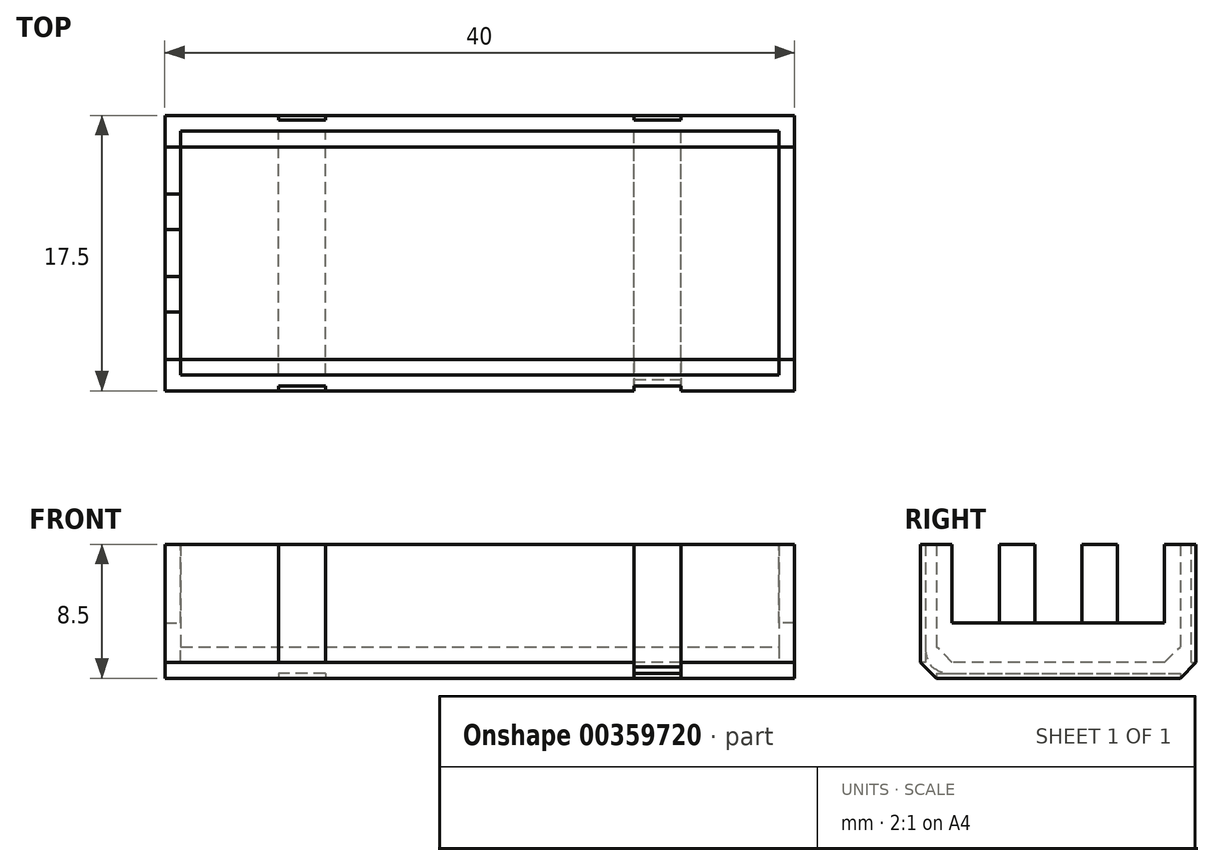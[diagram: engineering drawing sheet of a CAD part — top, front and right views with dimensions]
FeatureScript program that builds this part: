
annotation { "Feature Type Name" : "Feature", "Feature Type Description" : "" }
export const myFeature = defineFeature(function(context is Context, id is Id, definition is map)
    precondition{}
    {
        {
            var Q0;
            Q0=qCreatedBy(makeId("Top.planeOp"),FACE);
            var sketch = newSketch(context, id + "F0", { "sketchPlane" : qUnion([Q0])});
            skLineSegment(sketch, "E0.bottom", {"start": v(-85.67, 25.35) * mm, "end": v(-45.67, 25.35) * mm});
            skLineSegment(sketch, "E0.top", {"start": v(-85.67, 7.85) * mm, "end": v(-45.67, 7.85) * mm});
            skLineSegment(sketch, "E0.left", {"start": v(-85.67, 25.35) * mm, "end": v(-85.67, 7.85) * mm});
            skLineSegment(sketch, "E0.right", {"start": v(-45.67, 25.35) * mm, "end": v(-45.67, 7.85) * mm});
            skLineSegment(sketch, "E1", {"start": v(-65.67, 7.85) * mm, "end": v(-65.67, 25.35) * mm, "construction": true});
            skSolve(sketch);
        }
        {
            var Q0;
            Q0=qSketchRegion(id+"F0",true);
            extrude(context, id + "F1", {"entities" : qUnion([Q0]), "depth" : 8.5 * mm});
        }
        {
            var Q0;
            Q0=makeQuery(id+"F1.opExtrude","CAP_FACE",FACE,{"disambiguationData":[OSD([sQuery(id+"F0.wireOp",EDGE,"E0.bottom"),sQuery(id+"F0.wireOp",EDGE,"E0.top"),sQuery(id+"F0.wireOp",EDGE,"E0.left"),sQuery(id+"F0.wireOp",EDGE,"E0.right")])],"isStart":false});
            shell(context, id + "F2", {"entities" : qUnion([Q0]), "thickness" : 1 * mm});
        }
        {
            var Q0;
            Q0=makeQuery(id+"F1.opExtrude","CAP_FACE",FACE,{"disambiguationData":[OSD([sQuery(id+"F0.wireOp",EDGE,"E0.bottom"),sQuery(id+"F0.wireOp",EDGE,"E0.top"),sQuery(id+"F0.wireOp",EDGE,"E0.left"),sQuery(id+"F0.wireOp",EDGE,"E0.right")])],"isStart":false});
            var sketch = newSketch(context, id + "F3", { "sketchPlane" : qUnion([Q0])});
            skLineSegment(sketch, "E2", {"start": v(-85.67, 25.35) * mm, "end": v(-85.67, 23.35) * mm});
            skLineSegment(sketch, "E3", {"start": v(-85.67, 7.85) * mm, "end": v(-85.67, 9.85) * mm});
            skLineSegment(sketch, "E4.bottom", {"start": v(-85.67, 23.35) * mm, "end": v(-84.67, 23.35) * mm});
            skLineSegment(sketch, "E4.top", {"start": v(-85.67, 20.35) * mm, "end": v(-84.67, 20.35) * mm});
            skLineSegment(sketch, "E4.left", {"start": v(-85.67, 23.35) * mm, "end": v(-85.67, 20.35) * mm});
            skLineSegment(sketch, "E4.right", {"start": v(-84.67, 23.35) * mm, "end": v(-84.67, 20.35) * mm});
            skLineSegment(sketch, "E5.bottom", {"start": v(-85.67, 9.85) * mm, "end": v(-84.67, 9.85) * mm});
            skLineSegment(sketch, "E5.top", {"start": v(-85.67, 12.85) * mm, "end": v(-84.67, 12.85) * mm});
            skLineSegment(sketch, "E5.left", {"start": v(-85.67, 9.85) * mm, "end": v(-85.67, 12.85) * mm});
            skLineSegment(sketch, "E5.right", {"start": v(-84.67, 9.85) * mm, "end": v(-84.67, 12.85) * mm});
            skLineSegment(sketch, "E6.bottom", {"start": v(-85.67, 18.1) * mm, "end": v(-84.67, 18.1) * mm});
            skLineSegment(sketch, "E6.top", {"start": v(-85.67, 15.1) * mm, "end": v(-84.67, 15.1) * mm});
            skLineSegment(sketch, "E6.left", {"start": v(-85.67, 18.1) * mm, "end": v(-85.67, 15.1) * mm});
            skLineSegment(sketch, "E6.right", {"start": v(-84.67, 18.1) * mm, "end": v(-84.67, 15.1) * mm});
            skPoint(sketch, "E7", {"position": v(-84.67, 16.6) * mm});
            skPoint(sketch, "E8", {"position": v(-46.67, 16.6) * mm});
            skLineSegment(sketch, "E9", {"start": v(-65.67, 24.35) * mm, "end": v(-65.67, 8.85) * mm, "construction": true});
            skLineSegment(sketch, "E10.MirrorCS", {"start": v(-45.67, 23.35) * mm, "end": v(-46.67, 23.35) * mm});
            skLineSegment(sketch, "E11.MirrorCS", {"start": v(-45.67, 20.35) * mm, "end": v(-46.67, 20.35) * mm});
            skLineSegment(sketch, "E12.MirrorCS", {"start": v(-45.67, 23.35) * mm, "end": v(-45.67, 20.35) * mm});
            skLineSegment(sketch, "E13.MirrorCS", {"start": v(-46.67, 23.35) * mm, "end": v(-46.67, 20.35) * mm});
            skLineSegment(sketch, "E14.MirrorCS", {"start": v(-45.67, 9.85) * mm, "end": v(-46.67, 9.85) * mm});
            skLineSegment(sketch, "E15.MirrorCS", {"start": v(-45.67, 12.85) * mm, "end": v(-46.67, 12.85) * mm});
            skLineSegment(sketch, "E16.MirrorCS", {"start": v(-45.67, 9.85) * mm, "end": v(-45.67, 12.85) * mm});
            skLineSegment(sketch, "E17.MirrorCS", {"start": v(-46.67, 9.85) * mm, "end": v(-46.67, 12.85) * mm});
            skLineSegment(sketch, "E18.MirrorCS", {"start": v(-45.67, 18.1) * mm, "end": v(-45.67, 15.1) * mm});
            skLineSegment(sketch, "E19.MirrorCS", {"start": v(-46.67, 18.1) * mm, "end": v(-46.67, 15.1) * mm});
            skLineSegment(sketch, "E20.MirrorCS", {"start": v(-45.67, 15.1) * mm, "end": v(-46.67, 15.1) * mm});
            skLineSegment(sketch, "E21.MirrorCS", {"start": v(-45.67, 18.1) * mm, "end": v(-46.67, 18.1) * mm});
            skSolve(sketch);
        }
        {
            var Q0;
            Q0=makeQuery(id+"F3.imprint","IMPRINT",FACE,{"disambiguationData":[TD([[makeQuery(id+"F3.imprint","IMPRINT",EDGE,{"derivedFrom":sQuery(id+"F3.wireOp",EDGE,"E4.bottom")}),-1.0]])]});
            var Q1;
            Q1=makeQuery(id+"F3.imprint","IMPRINT",FACE,{"disambiguationData":[TD([[makeQuery(id+"F3.imprint","IMPRINT",EDGE,{"derivedFrom":sQuery(id+"F3.wireOp",EDGE,"E6.bottom")}),-1.0]])]});
            var Q2;
            Q2=makeQuery(id+"F3.imprint","IMPRINT",FACE,{"disambiguationData":[TD([[makeQuery(id+"F3.imprint","IMPRINT",EDGE,{"derivedFrom":sQuery(id+"F3.wireOp",EDGE,"E5.bottom")}),1.0]])]});
            var Q3;
            Q3=makeQuery(id+"F3.imprint","IMPRINT",FACE,{"disambiguationData":[TD([[makeQuery(id+"F3.imprint","IMPRINT",EDGE,{"derivedFrom":sQuery(id+"F3.wireOp",EDGE,"E14.MirrorCS")}),-1.0]])]});
            var Q4;
            Q4=makeQuery(id+"F3.imprint","IMPRINT",FACE,{"disambiguationData":[TD([[makeQuery(id+"F3.imprint","IMPRINT",EDGE,{"derivedFrom":sQuery(id+"F3.wireOp",EDGE,"E18.MirrorCS")}),-1.0]])]});
            var Q5;
            Q5=makeQuery(id+"F3.imprint","IMPRINT",FACE,{"disambiguationData":[TD([[makeQuery(id+"F3.imprint","IMPRINT",EDGE,{"derivedFrom":sQuery(id+"F3.wireOp",EDGE,"E10.MirrorCS")}),1.0]])]});
            extrude(context, id + "F4", {"entities" : qUnion([Q0, Q1, Q2, Q3, Q4, Q5]), "operationType" : NewBodyOperationType.REMOVE, "oppositeDirection" : true, "depth" : 5 * mm});
        }
        {
            var Q0;
            Q0=makeQuery(id+"F1.opExtrude","CAP_EDGE",EDGE,{"disambiguationData":[OSD([sQuery(id+"F0.wireOp",EDGE,"E0.top")])],"isStart":true});
            var Q1;
            {var subQ0=sQuery(id+"F0.wireOp",EDGE,"E0.top");var subQ1=sQuery(id+"F0.wireOp",EDGE,"E0.right");Q1=makeQuery(id+"F6hiMXC0ifSG0O5_1.opFillet","BLEND_EDGE",EDGE,{"blendedFrom":[makeQuery(id+"FY9jGdD6YKkP4tm_1.opChamfer","BLEND_EDGE",EDGE,{"blendedFrom":[makeQuery(id+"F1.opExtrude","CAP_EDGE",EDGE,{"disambiguationData":[OSD([subQ1])],"isStart":true}),makeQuery(id+"F1.opExtrude","CAP_FACE",FACE,{"disambiguationData":[OSD([sQuery(id+"F0.wireOp",EDGE,"E0.bottom"),subQ0,sQuery(id+"F0.wireOp",EDGE,"E0.left"),subQ1])],"isStart":true})],"blendedInto":[makeQuery(id+"F1.opExtrude","CAP_FACE",FACE,{"disambiguationData":[OSD([sQuery(id+"F0.wireOp",EDGE,"E0.bottom"),subQ0,sQuery(id+"F0.wireOp",EDGE,"E0.left"),subQ1])],"isStart":true})]}),makeQuery(id+"F1.opExtrude","SWEPT_FACE",FACE,{"disambiguationData":[OSD([subQ0])]})],"blendedInto":[makeQuery(id+"F1.opExtrude","SWEPT_FACE",FACE,{"disambiguationData":[OSD([subQ0])]})]});}
            var Q2;
            Q2=makeQuery(id+"FY9jGdD6YKkP4tm_1.opChamfer","BLEND_EDGE",EDGE,{"blendedFrom":[makeQuery(id+"F1.opExtrude","CAP_EDGE",EDGE,{"disambiguationData":[OSD([sQuery(id+"F0.wireOp",EDGE,"E0.right")])],"isStart":true}),makeQuery(id+"F1.opExtrude","SWEPT_FACE",FACE,{"disambiguationData":[OSD([sQuery(id+"F0.wireOp",EDGE,"E0.top")])]})],"blendedInto":[makeQuery(id+"F1.opExtrude","SWEPT_FACE",FACE,{"disambiguationData":[OSD([sQuery(id+"F0.wireOp",EDGE,"E0.top")])]})]});
            var Q3;
            {var subQ0=sQuery(id+"F0.wireOp",EDGE,"E0.top");var subQ1=sQuery(id+"F0.wireOp",EDGE,"E0.left");Q3=makeQuery(id+"F6hiMXC0ifSG0O5_1.opFillet","BLEND_EDGE",EDGE,{"blendedFrom":[makeQuery(id+"FY9jGdD6YKkP4tm_1.opChamfer","BLEND_EDGE",EDGE,{"blendedFrom":[makeQuery(id+"F1.opExtrude","CAP_EDGE",EDGE,{"disambiguationData":[OSD([subQ1])],"isStart":true}),makeQuery(id+"F1.opExtrude","CAP_FACE",FACE,{"disambiguationData":[OSD([sQuery(id+"F0.wireOp",EDGE,"E0.bottom"),subQ0,subQ1,sQuery(id+"F0.wireOp",EDGE,"E0.right")])],"isStart":true})],"blendedInto":[makeQuery(id+"F1.opExtrude","CAP_FACE",FACE,{"disambiguationData":[OSD([sQuery(id+"F0.wireOp",EDGE,"E0.bottom"),subQ0,subQ1,sQuery(id+"F0.wireOp",EDGE,"E0.right")])],"isStart":true})]}),makeQuery(id+"F1.opExtrude","SWEPT_FACE",FACE,{"disambiguationData":[OSD([subQ0])]})],"blendedInto":[makeQuery(id+"F1.opExtrude","SWEPT_FACE",FACE,{"disambiguationData":[OSD([subQ0])]})]});}
            var Q4;
            Q4=makeQuery(id+"FY9jGdD6YKkP4tm_1.opChamfer","BLEND_EDGE",EDGE,{"blendedFrom":[makeQuery(id+"F1.opExtrude","CAP_EDGE",EDGE,{"disambiguationData":[OSD([sQuery(id+"F0.wireOp",EDGE,"E0.left")])],"isStart":true}),makeQuery(id+"F1.opExtrude","SWEPT_FACE",FACE,{"disambiguationData":[OSD([sQuery(id+"F0.wireOp",EDGE,"E0.top")])]})],"blendedInto":[makeQuery(id+"F1.opExtrude","SWEPT_FACE",FACE,{"disambiguationData":[OSD([sQuery(id+"F0.wireOp",EDGE,"E0.top")])]})]});
            var Q5;
            Q5=makeQuery(id+"FY9jGdD6YKkP4tm_1.opChamfer","BLEND_EDGE",EDGE,{"blendedFrom":[makeQuery(id+"F1.opExtrude","CAP_EDGE",EDGE,{"disambiguationData":[OSD([sQuery(id+"F0.wireOp",EDGE,"E0.right")])],"isStart":true}),makeQuery(id+"F1.opExtrude","SWEPT_FACE",FACE,{"disambiguationData":[OSD([sQuery(id+"F0.wireOp",EDGE,"E0.bottom")])]})],"blendedInto":[makeQuery(id+"F1.opExtrude","SWEPT_FACE",FACE,{"disambiguationData":[OSD([sQuery(id+"F0.wireOp",EDGE,"E0.bottom")])]})]});
            var Q6;
            {var subQ0=sQuery(id+"F0.wireOp",EDGE,"E0.bottom");var subQ1=sQuery(id+"F0.wireOp",EDGE,"E0.right");Q6=makeQuery(id+"F6hiMXC0ifSG0O5_1.opFillet","BLEND_EDGE",EDGE,{"blendedFrom":[makeQuery(id+"FY9jGdD6YKkP4tm_1.opChamfer","BLEND_EDGE",EDGE,{"blendedFrom":[makeQuery(id+"F1.opExtrude","CAP_EDGE",EDGE,{"disambiguationData":[OSD([subQ1])],"isStart":true}),makeQuery(id+"F1.opExtrude","CAP_FACE",FACE,{"disambiguationData":[OSD([subQ0,sQuery(id+"F0.wireOp",EDGE,"E0.top"),sQuery(id+"F0.wireOp",EDGE,"E0.left"),subQ1])],"isStart":true})],"blendedInto":[makeQuery(id+"F1.opExtrude","CAP_FACE",FACE,{"disambiguationData":[OSD([subQ0,sQuery(id+"F0.wireOp",EDGE,"E0.top"),sQuery(id+"F0.wireOp",EDGE,"E0.left"),subQ1])],"isStart":true})]}),makeQuery(id+"F1.opExtrude","SWEPT_FACE",FACE,{"disambiguationData":[OSD([subQ0])]})],"blendedInto":[makeQuery(id+"F1.opExtrude","SWEPT_FACE",FACE,{"disambiguationData":[OSD([subQ0])]})]});}
            var Q7;
            Q7=makeQuery(id+"F1.opExtrude","CAP_EDGE",EDGE,{"disambiguationData":[OSD([sQuery(id+"F0.wireOp",EDGE,"E0.bottom")])],"isStart":true});
            var Q8;
            {var subQ0=sQuery(id+"F0.wireOp",EDGE,"E0.bottom");var subQ1=sQuery(id+"F0.wireOp",EDGE,"E0.left");Q8=makeQuery(id+"F6hiMXC0ifSG0O5_1.opFillet","BLEND_EDGE",EDGE,{"blendedFrom":[makeQuery(id+"FY9jGdD6YKkP4tm_1.opChamfer","BLEND_EDGE",EDGE,{"blendedFrom":[makeQuery(id+"F1.opExtrude","CAP_EDGE",EDGE,{"disambiguationData":[OSD([subQ1])],"isStart":true}),makeQuery(id+"F1.opExtrude","CAP_FACE",FACE,{"disambiguationData":[OSD([subQ0,sQuery(id+"F0.wireOp",EDGE,"E0.top"),subQ1,sQuery(id+"F0.wireOp",EDGE,"E0.right")])],"isStart":true})],"blendedInto":[makeQuery(id+"F1.opExtrude","CAP_FACE",FACE,{"disambiguationData":[OSD([subQ0,sQuery(id+"F0.wireOp",EDGE,"E0.top"),subQ1,sQuery(id+"F0.wireOp",EDGE,"E0.right")])],"isStart":true})]}),makeQuery(id+"F1.opExtrude","SWEPT_FACE",FACE,{"disambiguationData":[OSD([subQ0])]})],"blendedInto":[makeQuery(id+"F1.opExtrude","SWEPT_FACE",FACE,{"disambiguationData":[OSD([subQ0])]})]});}
            var Q9;
            Q9=makeQuery(id+"FY9jGdD6YKkP4tm_1.opChamfer","BLEND_EDGE",EDGE,{"blendedFrom":[makeQuery(id+"F1.opExtrude","CAP_EDGE",EDGE,{"disambiguationData":[OSD([sQuery(id+"F0.wireOp",EDGE,"E0.left")])],"isStart":true}),makeQuery(id+"F1.opExtrude","SWEPT_FACE",FACE,{"disambiguationData":[OSD([sQuery(id+"F0.wireOp",EDGE,"E0.bottom")])]})],"blendedInto":[makeQuery(id+"F1.opExtrude","SWEPT_FACE",FACE,{"disambiguationData":[OSD([sQuery(id+"F0.wireOp",EDGE,"E0.bottom")])]})]});
            chamfer(context, id + "F5", {"entities" : qUnion([Q0, Q1, Q2, Q3, Q4, Q5, Q6, Q7, Q8, Q9]), "width" : 1 * mm, "tangentPropagation" : true});
        }
        {
            var Q0;
            Q0=makeQuery(id+"F1.opExtrude","CAP_FACE",FACE,{"disambiguationData":[OSD([sQuery(id+"F0.wireOp",EDGE,"E0.bottom"),sQuery(id+"F0.wireOp",EDGE,"E0.top"),sQuery(id+"F0.wireOp",EDGE,"E0.left"),sQuery(id+"F0.wireOp",EDGE,"E0.right")])],"isStart":true});
            var sketch = newSketch(context, id + "F6", { "sketchPlane" : qUnion([Q0])});
            skLineSegment(sketch, "E22.bottom", {"start": v(-78.46, -8.85) * mm, "end": v(-75.46, -8.85) * mm});
            skLineSegment(sketch, "E22.top", {"start": v(-78.46, -24.35) * mm, "end": v(-75.46, -24.35) * mm});
            skLineSegment(sketch, "E22.left", {"start": v(-78.46, -8.85) * mm, "end": v(-78.46, -24.35) * mm});
            skLineSegment(sketch, "E22.right", {"start": v(-75.46, -8.85) * mm, "end": v(-75.46, -24.35) * mm});
            skLineSegment(sketch, "E23.MirrorCS", {"start": v(-52.88, -8.85) * mm, "end": v(-52.88, -24.35) * mm});
            skLineSegment(sketch, "E24.MirrorCS", {"start": v(-52.88, -8.85) * mm, "end": v(-55.88, -8.85) * mm});
            skLineSegment(sketch, "E25.MirrorCS", {"start": v(-52.88, -24.35) * mm, "end": v(-55.88, -24.35) * mm});
            skLineSegment(sketch, "E26.MirrorCS", {"start": v(-55.88, -8.85) * mm, "end": v(-55.88, -24.35) * mm});
            skSolve(sketch);
        }
        {
            var Q0;
            Q0=makeQuery(id+"F5.opChamfer","BLEND_FACE",FACE,{"disambiguationData":[OSD([sQuery(id+"F0.wireOp",EDGE,"E0.bottom")])]});
            var sketch = newSketch(context, id + "F7", { "sketchPlane" : qUnion([Q0])});
            skLineSegment(sketch, "E27.0.0", {"start": v(-75.46, -17.22) * mm, "end": v(-75.46, -6.26) * mm});
            skLineSegment(sketch, "E27.0.1", {"start": v(-75.46, -6.26) * mm, "end": v(-78.46, -6.26) * mm});
            skLineSegment(sketch, "E27.0.2", {"start": v(-78.46, -6.26) * mm, "end": v(-78.46, -17.22) * mm});
            skLineSegment(sketch, "E27.0.3", {"start": v(-78.46, -17.22) * mm, "end": v(-75.46, -17.22) * mm});
            skLineSegment(sketch, "E28.left", {"start": v(-78.46, -17.22) * mm, "end": v(-78.46, -17.22) * mm});
            skLineSegment(sketch, "E28.right", {"start": v(-75.46, -17.22) * mm, "end": v(-75.46, -17.22) * mm});
            skLineSegment(sketch, "E29.bottom", {"start": v(-75.46, -18.63) * mm, "end": v(-78.46, -18.63) * mm});
            skLineSegment(sketch, "E29.top", {"start": v(-75.46, -17.22) * mm, "end": v(-78.46, -17.22) * mm});
            skLineSegment(sketch, "E29.left", {"start": v(-75.46, -18.63) * mm, "end": v(-75.46, -17.22) * mm});
            skLineSegment(sketch, "E29.right", {"start": v(-78.46, -18.63) * mm, "end": v(-78.46, -17.22) * mm});
            skLineSegment(sketch, "E30.MirrorCS", {"start": v(-52.88, -17.22) * mm, "end": v(-55.88, -17.22) * mm});
            skLineSegment(sketch, "E31.MirrorCS", {"start": v(-52.88, -18.63) * mm, "end": v(-52.88, -17.22) * mm});
            skLineSegment(sketch, "E32.MirrorCS", {"start": v(-55.88, -18.63) * mm, "end": v(-55.88, -17.22) * mm});
            skLineSegment(sketch, "E33.MirrorCS", {"start": v(-55.88, -18.63) * mm, "end": v(-52.88, -18.63) * mm});
            skLineSegment(sketch, "E34.MirrorCS", {"start": v(-55.88, -17.22) * mm, "end": v(-52.88, -17.22) * mm});
            skSolve(sketch);
        }
        {
            var Q0;
            Q0=makeQuery(id+"F1.opExtrude","SWEPT_FACE",FACE,{"disambiguationData":[OSD([sQuery(id+"F0.wireOp",EDGE,"E0.bottom")])]});
            var sketch = newSketch(context, id + "F8", { "sketchPlane" : qUnion([Q0])});
            skLineSegment(sketch, "E35.0.0", {"start": v(78.46, 0) * mm, "end": v(78.46, 1) * mm});
            skLineSegment(sketch, "E35.0.1", {"start": v(78.46, 1) * mm, "end": v(75.46, 1) * mm});
            skLineSegment(sketch, "E35.0.2", {"start": v(75.46, 1) * mm, "end": v(75.46, 0) * mm});
            skLineSegment(sketch, "E35.0.3", {"start": v(75.46, 0) * mm, "end": v(78.46, 0) * mm});
            skLineSegment(sketch, "E36.top", {"start": v(78.46, 8.5) * mm, "end": v(75.46, 8.5) * mm});
            skLineSegment(sketch, "E36.left", {"start": v(78.46, 1) * mm, "end": v(78.46, 8.5) * mm});
            skLineSegment(sketch, "E36.right", {"start": v(75.46, 1) * mm, "end": v(75.46, 8.5) * mm});
            skLineSegment(sketch, "E37", {"start": v(65.67, 1) * mm, "end": v(65.67, 8.5) * mm, "construction": true});
            skLineSegment(sketch, "E38.MirrorCS", {"start": v(52.88, 1) * mm, "end": v(55.88, 1) * mm});
            skLineSegment(sketch, "E39.MirrorCS", {"start": v(52.88, 1) * mm, "end": v(52.88, 8.5) * mm});
            skLineSegment(sketch, "E40.MirrorCS", {"start": v(55.88, 1) * mm, "end": v(55.88, 8.5) * mm});
            skLineSegment(sketch, "E41.MirrorCS", {"start": v(52.88, 8.5) * mm, "end": v(55.88, 8.5) * mm});
            skSolve(sketch);
        }
        {
            var Q0;
            Q0=makeQuery(id+"F1.opExtrude","SWEPT_FACE",FACE,{"disambiguationData":[OSD([sQuery(id+"F0.wireOp",EDGE,"E0.top")])]});
            var sketch = newSketch(context, id + "F9", { "sketchPlane" : qUnion([Q0])});
            skLineSegment(sketch, "E42.0.0", {"start": v(-75.46, 8.5) * mm, "end": v(-75.46, 1) * mm});
            skLineSegment(sketch, "E42.0.1", {"start": v(-75.46, 1) * mm, "end": v(-78.46, 1) * mm});
            skLineSegment(sketch, "E42.0.2", {"start": v(-78.46, 1) * mm, "end": v(-78.46, 8.5) * mm});
            skLineSegment(sketch, "E42.0.3", {"start": v(-78.46, 8.5) * mm, "end": v(-75.46, 8.5) * mm});
            skLineSegment(sketch, "E43", {"start": v(-65.67, 1) * mm, "end": v(-65.67, 8.5) * mm, "construction": true});
            skLineSegment(sketch, "E44.MirrorCS", {"start": v(-55.88, 1) * mm, "end": v(-52.88, 1) * mm});
            skLineSegment(sketch, "E45.MirrorCS", {"start": v(-55.88, 8.5) * mm, "end": v(-55.88, 1) * mm});
            skLineSegment(sketch, "E46.MirrorCS", {"start": v(-52.88, 8.5) * mm, "end": v(-55.88, 8.5) * mm});
            skLineSegment(sketch, "E47.MirrorCS", {"start": v(-52.88, 1) * mm, "end": v(-52.88, 8.5) * mm});
            skSolve(sketch);
        }
        {
            var Q0;
            Q0=makeQuery(id+"F5.opChamfer","BLEND_FACE",FACE,{"disambiguationData":[OSD([sQuery(id+"F0.wireOp",EDGE,"E0.top")])]});
            var sketch = newSketch(context, id + "F10", { "sketchPlane" : qUnion([Q0])});
            skLineSegment(sketch, "E48.0.0", {"start": v(-78.46, 0.46) * mm, "end": v(-78.46, -4.84) * mm});
            skLineSegment(sketch, "E48.0.1", {"start": v(-78.46, -4.84) * mm, "end": v(-75.46, -4.84) * mm});
            skLineSegment(sketch, "E48.0.2", {"start": v(-75.46, -4.84) * mm, "end": v(-75.46, 0.46) * mm});
            skLineSegment(sketch, "E48.0.3", {"start": v(-75.46, 0.46) * mm, "end": v(-78.46, 0.46) * mm});
            skLineSegment(sketch, "E49.bottom", {"start": v(-75.46, -4.84) * mm, "end": v(-78.46, -4.84) * mm});
            skLineSegment(sketch, "E49.top", {"start": v(-75.46, -6.26) * mm, "end": v(-78.46, -6.26) * mm});
            skLineSegment(sketch, "E49.left", {"start": v(-75.46, -4.84) * mm, "end": v(-75.46, -6.26) * mm});
            skLineSegment(sketch, "E49.right", {"start": v(-78.46, -4.84) * mm, "end": v(-78.46, -6.26) * mm});
            skLineSegment(sketch, "E50.MirrorCS", {"start": v(-52.88, -4.84) * mm, "end": v(-55.88, -4.84) * mm});
            skLineSegment(sketch, "E51.MirrorCS", {"start": v(-52.88, -4.84) * mm, "end": v(-52.88, -6.26) * mm});
            skLineSegment(sketch, "E52.MirrorCS", {"start": v(-55.88, -4.84) * mm, "end": v(-55.88, -6.26) * mm});
            skLineSegment(sketch, "E53.MirrorCS", {"start": v(-55.88, -4.84) * mm, "end": v(-52.88, -4.84) * mm});
            skLineSegment(sketch, "E54.MirrorCS", {"start": v(-55.88, -6.26) * mm, "end": v(-52.88, -6.26) * mm});
            skSolve(sketch);
        }
        {
            var Q0;
            Q0=makeQuery(id+"F8.imprint","IMPRINT",FACE,{"disambiguationData":[TD([[makeQuery(id+"F8.imprint","IMPRINT",EDGE,{"derivedFrom":sQuery(id+"F8.wireOp",EDGE,"E35.0.1")}),1.0]])]});
            var Q1;
            Q1=makeQuery(id+"F8.imprint","IMPRINT",FACE,{"disambiguationData":[TD([[makeQuery(id+"F8.imprint","IMPRINT",EDGE,{"derivedFrom":sQuery(id+"F8.wireOp",EDGE,"E39.MirrorCS")}),-1.0]])]});
            extrude(context, id + "F11", {"entities" : qUnion([Q0, Q1]), "operationType" : NewBodyOperationType.REMOVE, "oppositeDirection" : true, "depth" : .3 * mm});
        }
        {
            var Q0;
            Q0=makeQuery(id+"F7.imprint","IMPRINT",FACE,{"disambiguationData":[TD([[makeQuery(id+"F7.imprint","IMPRINT",EDGE,{"derivedFrom":sQuery(id+"F7.wireOp",EDGE,"E29.bottom")}),-1.0]])]});
            var Q1;
            Q1=makeQuery(id+"F7.imprint","IMPRINT",FACE,{"disambiguationData":[TD([[makeQuery(id+"F7.imprint","IMPRINT",EDGE,{"derivedFrom":sQuery(id+"F7.wireOp",EDGE,"E31.MirrorCS")}),1.0]])]});
            extrude(context, id + "F12", {"entities" : qUnion([Q0, Q1]), "operationType" : NewBodyOperationType.REMOVE, "oppositeDirection" : true, "depth" : 0.3 * mm});
        }
        {
            var Q0;
            Q0=makeQuery(id+"F6.imprint","IMPRINT",FACE,{"disambiguationData":[TD([[makeQuery(id+"F6.imprint","IMPRINT",EDGE,{"derivedFrom":sQuery(id+"F6.wireOp",EDGE,"E22.bottom")}),1.0]])]});
            var Q1;
            Q1=makeQuery(id+"F6.imprint","IMPRINT",FACE,{"disambiguationData":[TD([[makeQuery(id+"F6.imprint","IMPRINT",EDGE,{"derivedFrom":sQuery(id+"F6.wireOp",EDGE,"E23.MirrorCS")}),-1.0]])]});
            extrude(context, id + "F13", {"entities" : qUnion([Q0, Q1]), "operationType" : NewBodyOperationType.REMOVE, "oppositeDirection" : true, "depth" : 0.3 * mm});
        }
        {
            var Q0;
            Q0=makeQuery(id+"F9.imprint","IMPRINT",FACE,{"disambiguationData":[TD([[makeQuery(id+"F9.imprint","IMPRINT",EDGE,{"derivedFrom":sQuery(id+"F9.wireOp",EDGE,"E42.0.0")}),-1.0]])]});
            var Q1;
            Q1=makeQuery(id+"F9.imprint","IMPRINT",FACE,{"disambiguationData":[TD([[makeQuery(id+"F9.imprint","IMPRINT",EDGE,{"derivedFrom":sQuery(id+"F9.wireOp",EDGE,"E44.MirrorCS")}),1.0]])]});
            extrude(context, id + "F14", {"entities" : qUnion([Q0, Q1]), "operationType" : NewBodyOperationType.REMOVE, "oppositeDirection" : true, "depth" : 0.3 * mm});
        }
        {
            var Q0;
            Q0=makeQuery(id+"F10.imprint","IMPRINT",FACE,{"disambiguationData":[TD([[makeQuery(id+"F10.imprint","IMPRINT",EDGE,{"derivedFrom":sQuery(id+"F10.wireOp",EDGE,"E49.bottom")}),-1.0]])]});
            var Q1;
            Q1=makeQuery(id+"F10.imprint","IMPRINT",FACE,{"disambiguationData":[TD([[makeQuery(id+"F10.imprint","IMPRINT",EDGE,{"derivedFrom":sQuery(id+"F10.wireOp",EDGE,"E51.MirrorCS")}),-1.0]])]});
            extrude(context, id + "F15", {"entities" : qUnion([Q0, Q1]), "operationType" : NewBodyOperationType.REMOVE, "oppositeDirection" : true, "depth" : 0.3 * mm});
        }
        {
            var Q0;
            Q0=makeQuery(id+"F15.boolean.opBoolean","INTERSECT",EDGE,{"derivedFrom":[makeQuery(id+"F14.boolean.opBoolean","COPY",FACE,{"derivedFrom":makeQuery(id+"F14.opExtrude","CAP_FACE",FACE,{"disambiguationData":[OSD([sQuery(id+"F9.wireOp",EDGE,"E44.MirrorCS"),sQuery(id+"F9.wireOp",EDGE,"E45.MirrorCS"),sQuery(id+"F9.wireOp",EDGE,"E46.MirrorCS"),sQuery(id+"F9.wireOp",EDGE,"E47.MirrorCS")])],"isStart":false})}),makeQuery(id+"F15.opExtrude","CAP_FACE",FACE,{"disambiguationData":[OSD([sQuery(id+"F10.wireOp",EDGE,"E51.MirrorCS"),sQuery(id+"F10.wireOp",EDGE,"E52.MirrorCS"),sQuery(id+"F10.wireOp",EDGE,"E53.MirrorCS"),sQuery(id+"F10.wireOp",EDGE,"E54.MirrorCS")])],"isStart":false})]});
            var Q1;
            Q1=makeQuery(id+"F15.boolean.opBoolean","INTERSECT",EDGE,{"derivedFrom":[makeQuery(id+"F13.boolean.opBoolean","COPY",FACE,{"derivedFrom":makeQuery(id+"F13.opExtrude","CAP_FACE",FACE,{"disambiguationData":[OSD([sQuery(id+"F6.wireOp",EDGE,"E23.MirrorCS"),sQuery(id+"F6.wireOp",EDGE,"E24.MirrorCS"),sQuery(id+"F6.wireOp",EDGE,"E25.MirrorCS"),sQuery(id+"F6.wireOp",EDGE,"E26.MirrorCS")])],"isStart":false})}),makeQuery(id+"F15.opExtrude","CAP_FACE",FACE,{"disambiguationData":[OSD([sQuery(id+"F10.wireOp",EDGE,"E51.MirrorCS"),sQuery(id+"F10.wireOp",EDGE,"E52.MirrorCS"),sQuery(id+"F10.wireOp",EDGE,"E53.MirrorCS"),sQuery(id+"F10.wireOp",EDGE,"E54.MirrorCS")])],"isStart":false})]});
            var Q2;
            Q2=makeQuery(id+"F15.boolean.opBoolean","INTERSECT",EDGE,{"derivedFrom":[makeQuery(id+"F13.boolean.opBoolean","COPY",FACE,{"derivedFrom":makeQuery(id+"F13.opExtrude","CAP_FACE",FACE,{"disambiguationData":[OSD([sQuery(id+"F6.wireOp",EDGE,"E22.bottom"),sQuery(id+"F6.wireOp",EDGE,"E22.top"),sQuery(id+"F6.wireOp",EDGE,"E22.left"),sQuery(id+"F6.wireOp",EDGE,"E22.right")])],"isStart":false})}),makeQuery(id+"F15.opExtrude","CAP_FACE",FACE,{"disambiguationData":[OSD([sQuery(id+"F10.wireOp",EDGE,"E49.bottom"),sQuery(id+"F10.wireOp",EDGE,"E49.top"),sQuery(id+"F10.wireOp",EDGE,"E49.left"),sQuery(id+"F10.wireOp",EDGE,"E49.right")])],"isStart":false})]});
            var Q3;
            Q3=makeQuery(id+"F15.boolean.opBoolean","INTERSECT",EDGE,{"derivedFrom":[makeQuery(id+"F14.boolean.opBoolean","COPY",FACE,{"derivedFrom":makeQuery(id+"F14.opExtrude","CAP_FACE",FACE,{"disambiguationData":[OSD([sQuery(id+"F9.wireOp",EDGE,"E42.0.0"),sQuery(id+"F9.wireOp",EDGE,"E42.0.1"),sQuery(id+"F9.wireOp",EDGE,"E42.0.2"),sQuery(id+"F9.wireOp",EDGE,"E42.0.3")])],"isStart":false})}),makeQuery(id+"F15.opExtrude","CAP_FACE",FACE,{"disambiguationData":[OSD([sQuery(id+"F10.wireOp",EDGE,"E49.bottom"),sQuery(id+"F10.wireOp",EDGE,"E49.top"),sQuery(id+"F10.wireOp",EDGE,"E49.left"),sQuery(id+"F10.wireOp",EDGE,"E49.right")])],"isStart":false})]});
            var Q4;
            Q4=makeQuery(id+"F13.boolean.opBoolean","INTERSECT",EDGE,{"derivedFrom":[makeQuery(id+"F12.boolean.opBoolean","COPY",FACE,{"derivedFrom":makeQuery(id+"F12.opExtrude","CAP_FACE",FACE,{"disambiguationData":[OSD([sQuery(id+"F7.wireOp",EDGE,"E29.bottom"),sQuery(id+"F7.wireOp",EDGE,"E29.top"),sQuery(id+"F7.wireOp",EDGE,"E29.left"),sQuery(id+"F7.wireOp",EDGE,"E29.right")])],"isStart":false})}),makeQuery(id+"F13.opExtrude","CAP_FACE",FACE,{"disambiguationData":[OSD([sQuery(id+"F6.wireOp",EDGE,"E22.bottom"),sQuery(id+"F6.wireOp",EDGE,"E22.top"),sQuery(id+"F6.wireOp",EDGE,"E22.left"),sQuery(id+"F6.wireOp",EDGE,"E22.right")])],"isStart":false})]});
            var Q5;
            Q5=makeQuery(id+"F12.boolean.opBoolean","INTERSECT",EDGE,{"derivedFrom":[makeQuery(id+"F11.boolean.opBoolean","COPY",FACE,{"derivedFrom":makeQuery(id+"F11.opExtrude","CAP_FACE",FACE,{"disambiguationData":[OSD([sQuery(id+"F8.wireOp",EDGE,"E35.0.1"),sQuery(id+"F8.wireOp",EDGE,"E36.top"),sQuery(id+"F8.wireOp",EDGE,"E36.left"),sQuery(id+"F8.wireOp",EDGE,"E36.right")])],"isStart":false})}),makeQuery(id+"F12.opExtrude","CAP_FACE",FACE,{"disambiguationData":[OSD([sQuery(id+"F7.wireOp",EDGE,"E29.bottom"),sQuery(id+"F7.wireOp",EDGE,"E29.top"),sQuery(id+"F7.wireOp",EDGE,"E29.left"),sQuery(id+"F7.wireOp",EDGE,"E29.right")])],"isStart":false})]});
            var Q6;
            Q6=makeQuery(id+"F12.boolean.opBoolean","INTERSECT",EDGE,{"derivedFrom":[makeQuery(id+"F11.boolean.opBoolean","COPY",FACE,{"derivedFrom":makeQuery(id+"F11.opExtrude","CAP_FACE",FACE,{"disambiguationData":[OSD([sQuery(id+"F8.wireOp",EDGE,"E39.MirrorCS"),sQuery(id+"F8.wireOp",EDGE,"E40.MirrorCS"),sQuery(id+"F8.wireOp",EDGE,"E38.MirrorCS"),sQuery(id+"F8.wireOp",EDGE,"E41.MirrorCS")])],"isStart":false})}),makeQuery(id+"F12.opExtrude","CAP_FACE",FACE,{"disambiguationData":[OSD([sQuery(id+"F7.wireOp",EDGE,"E31.MirrorCS"),sQuery(id+"F7.wireOp",EDGE,"E32.MirrorCS"),sQuery(id+"F7.wireOp",EDGE,"E33.MirrorCS"),sQuery(id+"F7.wireOp",EDGE,"E34.MirrorCS")])],"isStart":false})]});
            var Q7;
            Q7=makeQuery(id+"F13.boolean.opBoolean","INTERSECT",EDGE,{"derivedFrom":[makeQuery(id+"F12.boolean.opBoolean","COPY",FACE,{"derivedFrom":makeQuery(id+"F12.opExtrude","CAP_FACE",FACE,{"disambiguationData":[OSD([sQuery(id+"F7.wireOp",EDGE,"E31.MirrorCS"),sQuery(id+"F7.wireOp",EDGE,"E32.MirrorCS"),sQuery(id+"F7.wireOp",EDGE,"E33.MirrorCS"),sQuery(id+"F7.wireOp",EDGE,"E34.MirrorCS")])],"isStart":false})}),makeQuery(id+"F13.opExtrude","CAP_FACE",FACE,{"disambiguationData":[OSD([sQuery(id+"F6.wireOp",EDGE,"E23.MirrorCS"),sQuery(id+"F6.wireOp",EDGE,"E24.MirrorCS"),sQuery(id+"F6.wireOp",EDGE,"E25.MirrorCS"),sQuery(id+"F6.wireOp",EDGE,"E26.MirrorCS")])],"isStart":false})]});
            fillet(context, id + "F16", {"entities" : qUnion([Q0, Q1, Q2, Q3, Q4, Q5, Q6, Q7]), "radius" : 2 * mm, "tangentPropagation" : true, "allowEdgeOverflow" : false});
        }
        {
            var Q0;
            {var subQ0=sQuery(id+"F0.wireOp",EDGE,"E0.bottom");Q0=makeQuery(id+"F2.opShell","OFFSET_EDGE",EDGE,{"disambiguationData":[OSD([subQ0]),TDD([makeQuery(id+"F1.opExtrude","CAP_EDGE",EDGE,{"disambiguationData":[OSD([subQ0])],"isStart":true})])]});}
            var Q1;
            {var subQ0=sQuery(id+"F0.wireOp",EDGE,"E0.top");Q1=makeQuery(id+"F2.opShell","OFFSET_EDGE",EDGE,{"disambiguationData":[OSD([subQ0]),TDD([makeQuery(id+"F1.opExtrude","CAP_EDGE",EDGE,{"disambiguationData":[OSD([subQ0])],"isStart":true})])]});}
            chamfer(context, id + "F17", {"entities" : qUnion([Q0, Q1]), "width" : 1 * mm, "tangentPropagation" : true});
        }
        {
            var Q0;
            Q0=makeQuery(id+"F1.opExtrude","SWEPT_FACE",FACE,{"disambiguationData":[OSD([sQuery(id+"F0.wireOp",EDGE,"E0.right")])]});
            var sketch = newSketch(context, id + "F18", { "sketchPlane" : qUnion([Q0])});
            skLineSegment(sketch, "E55.bottom", {"start": v(12.85, 8.5) * mm, "end": v(15.1, 8.5) * mm});
            skLineSegment(sketch, "E55.top", {"start": v(12.85, 3.5) * mm, "end": v(15.1, 3.5) * mm});
            skLineSegment(sketch, "E55.left", {"start": v(12.85, 8.5) * mm, "end": v(12.85, 3.5) * mm});
            skLineSegment(sketch, "E55.right", {"start": v(15.1, 8.5) * mm, "end": v(15.1, 3.5) * mm});
            skLineSegment(sketch, "E56.bottom", {"start": v(18.1, 8.5) * mm, "end": v(20.35, 8.5) * mm});
            skLineSegment(sketch, "E56.top", {"start": v(18.1, 3.5) * mm, "end": v(20.35, 3.5) * mm});
            skLineSegment(sketch, "E56.left", {"start": v(18.1, 8.5) * mm, "end": v(18.1, 3.5) * mm});
            skLineSegment(sketch, "E56.right", {"start": v(20.35, 8.5) * mm, "end": v(20.35, 3.5) * mm});
            skSolve(sketch);
        }
        {
            var Q0;
            Q0=makeQuery(id+"F18.imprint","IMPRINT",FACE,{"disambiguationData":[TD([[makeQuery(id+"F18.imprint","IMPRINT",EDGE,{"derivedFrom":sQuery(id+"F18.wireOp",EDGE,"E55.bottom")}),1.0]])]});
            var Q1;
            Q1=makeQuery(id+"F18.imprint","IMPRINT",FACE,{"disambiguationData":[TD([[makeQuery(id+"F18.imprint","IMPRINT",EDGE,{"derivedFrom":sQuery(id+"F18.wireOp",EDGE,"E56.bottom")}),1.0]])]});
            extrude(context, id + "F19", {"entities" : qUnion([Q0, Q1]), "operationType" : NewBodyOperationType.REMOVE, "oppositeDirection" : true, "depth" : 25 * mm});
        }
    });
